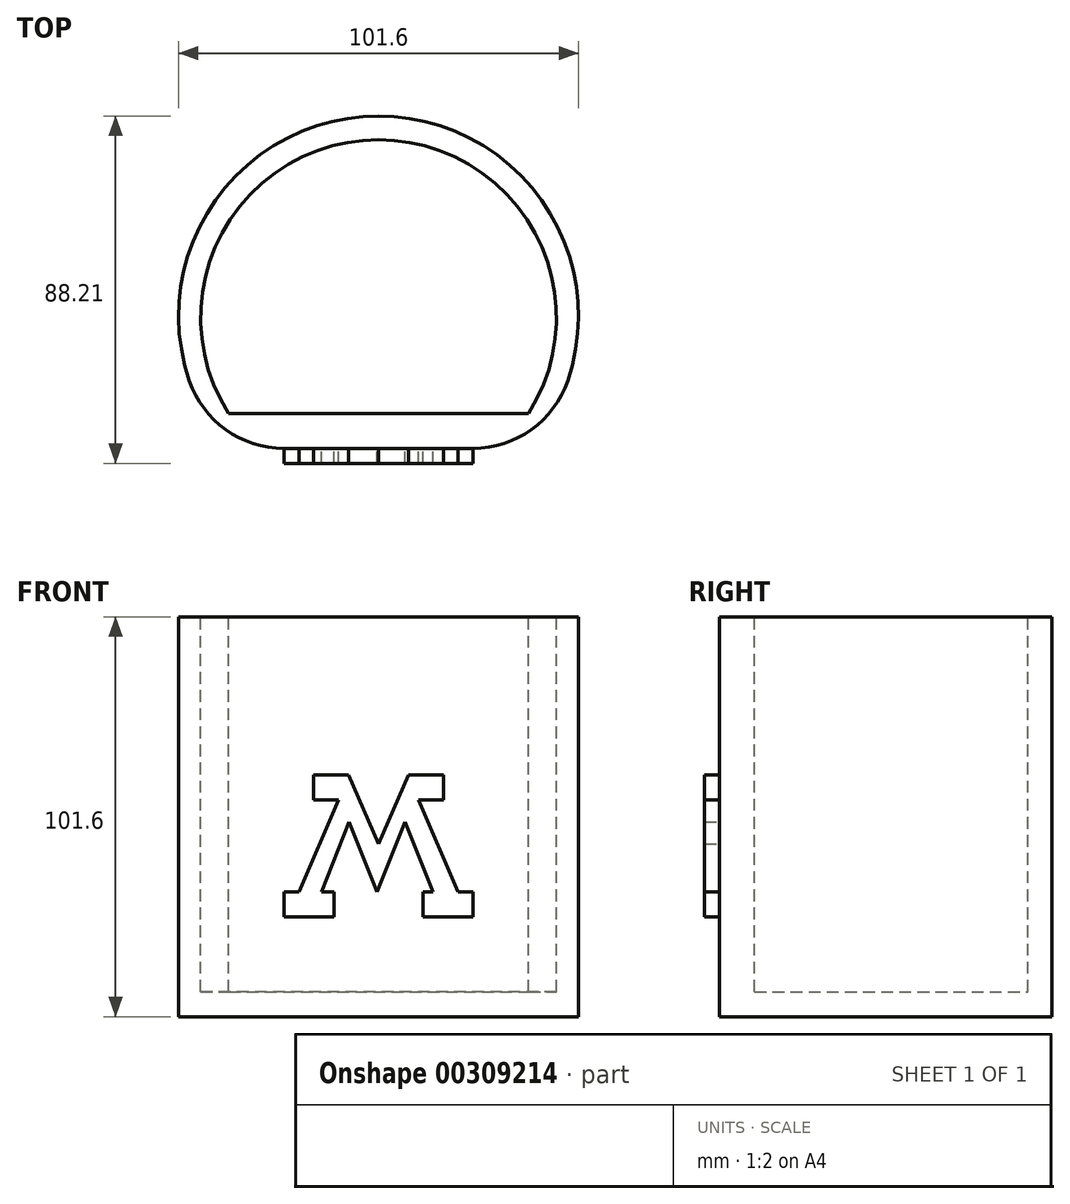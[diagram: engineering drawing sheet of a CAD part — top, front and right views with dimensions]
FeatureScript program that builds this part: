
annotation { "Feature Type Name" : "Feature", "Feature Type Description" : "" }
export const myFeature = defineFeature(function(context is Context, id is Id, definition is map)
    precondition{}
    {
        {
            var Q0;
            Q0=qCreatedBy(makeId("Top.planeOp"),FACE);
            var sketch = newSketch(context, id + "F0", { "sketchPlane" : qUnion([Q0])});
            skLineSegment(sketch, "E0", {"start": v(-42.3, 0) * mm, "end": v(33.9, 0) * mm});
            skArc(sketch, "E1", {"start": v(33.9, 0) * mm, "mid": v(-4.2, 84.4) * mm, "end": v(-42.3, 0) * mm});
            skSolve(sketch);
        }
        {
            var Q0;
            Q0=makeQuery(id+"F0.imprint","IMPRINT",FACE,{"disambiguationData":[TD([[makeQuery(id+"F0.imprint","IMPRINT",EDGE,{"derivedFrom":sQuery(id+"F0.wireOp",EDGE,"E0")}),1.0]])]});
            extrude(context, id + "F1", {"entities" : qUnion([Q0]), "depth" : 101.6 * mm});
        }
        {
            var Q0;
            Q0=makeQuery(id+"F1.opExtrude","CAP_FACE",FACE,{"disambiguationData":[OSD([sQuery(id+"F0.wireOp",EDGE,"E0"),sQuery(id+"F0.wireOp",EDGE,"E1")])],"isStart":false});
            var sketch = newSketch(context, id + "F2", { "sketchPlane" : qUnion([Q0])});
            skLineSegment(sketch, "E2", {"start": v(-42.3, 8.9) * mm, "end": v(33.9, 8.9) * mm});
            skArc(sketch, "E3", {"start": v(33.9, 8.9) * mm, "mid": v(-4.2, 78.39) * mm, "end": v(-42.3, 8.9) * mm});
            skSolve(sketch);
        }
        {
            var Q0;
            Q0=makeQuery(id+"F2.imprint","IMPRINT",FACE,{"disambiguationData":[TD([[makeQuery(id+"F2.imprint","IMPRINT",EDGE,{"derivedFrom":sQuery(id+"F2.wireOp",EDGE,"EuxJ9lTJ-i6S2-fETs-Mgd1-tVgnAVQvERU8")}),1.0]])]});
            var Q1;
            Q1=makeQuery(id+"F2.imprint","IMPRINT",FACE,{"disambiguationData":[TD([[makeQuery(id+"F2.imprint","IMPRINT",EDGE,{"derivedFrom":sQuery(id+"F2.wireOp",EDGE,"E2")}),1.0]])]});
            extrude(context, id + "F3", {"entities" : qUnion([Q0, Q1]), "operationType" : NewBodyOperationType.REMOVE, "oppositeDirection" : true, "depth" : 95.25 * mm});
        }
        {
            var Q0;
            {var subQ0=sQuery(id+"F0.wireOp",EDGE,"E1");var subQ1=sQuery(id+"F0.wireOp",EDGE,"E0");Q0=makeQuery(id+"F1.opExtrude","SWEPT_EDGE",EDGE,{"disambiguationData":[OSD([subQ1,subQ0]),TDD([makeQuery(id+"F0.imprint","INTERSECT",VERTEX,{"disambiguationData":[OD(0.0)],"derivedFrom":[subQ1,subQ0]})])]});}
            var Q1;
            {var subQ0=sQuery(id+"F0.wireOp",EDGE,"E1");var subQ1=sQuery(id+"F0.wireOp",EDGE,"E0");Q1=makeQuery(id+"F1.opExtrude","SWEPT_EDGE",EDGE,{"disambiguationData":[OSD([subQ1,subQ0]),TDD([makeQuery(id+"F0.imprint","INTERSECT",VERTEX,{"disambiguationData":[OD(1.0)],"derivedFrom":[subQ1,subQ0]})])]});}
            fillet(context, id + "F4", {"entities" : qUnion([Q0, Q1]), "radius" : 25.4 * mm, "tangentPropagation" : true, "allowEdgeOverflow" : false});
        }
        {
            var Q0;
            Q0=makeQuery(id+"F1.opExtrude","SWEPT_FACE",FACE,{"disambiguationData":[OSD([sQuery(id+"F0.wireOp",EDGE,"E0")])]});
            var sketch = newSketch(context, id + "F5", { "sketchPlane" : qUnion([Q0])});
            skPoint(sketch, "E4.endSnap0", {"position": v(19.83, 50.8) * mm});
            skLineSegment(sketch, "E5", {"start": v(-28.25, 0) * mm, "end": v(-28.25, 25.4) * mm});
            skLineSegment(sketch, "E6", {"start": v(-28.25, 25.4) * mm, "end": v(-15.55, 25.4) * mm});
            skLineSegment(sketch, "E7", {"start": v(-15.55, 25.4) * mm, "end": v(-15.55, 31.75) * mm});
            skLineSegment(sketch, "E8", {"start": v(-15.55, 31.75) * mm, "end": v(-18.74, 31.75) * mm});
            skLineSegment(sketch, "E9", {"start": v(19.83, 0) * mm, "end": v(19.83, 25.4) * mm});
            skLineSegment(sketch, "E10", {"start": v(19.83, 25.4) * mm, "end": v(7.13, 25.4) * mm});
            skPoint(sketch, "E10.endSnap0", {"position": v(-21.9, 25.4) * mm});
            skLineSegment(sketch, "E11", {"start": v(7.13, 25.4) * mm, "end": v(7.13, 31.75) * mm});
            skLineSegment(sketch, "E12", {"start": v(7.13, 31.75) * mm, "end": v(9.64, 31.75) * mm});
            skLineSegment(sketch, "E13", {"start": v(-18.74, 31.75) * mm, "end": v(-11.64, 49.43) * mm});
            skLineSegment(sketch, "E14", {"start": v(-11.64, 49.43) * mm, "end": v(-4.55, 31.75) * mm});
            skLineSegment(sketch, "E15", {"start": v(-4.55, 31.75) * mm, "end": v(2.55, 49.43) * mm});
            skLineSegment(sketch, "E16", {"start": v(2.55, 49.43) * mm, "end": v(9.64, 31.75) * mm});
            skLineSegment(sketch, "E17", {"start": v(-28.25, 25.4) * mm, "end": v(-28.25, 31.75) * mm});
            skLineSegment(sketch, "E18", {"start": v(-28.25, 31.75) * mm, "end": v(-24.44, 31.75) * mm});
            skLineSegment(sketch, "E19", {"start": v(-24.44, 31.75) * mm, "end": v(-14.33, 55.05) * mm});
            skLineSegment(sketch, "E20", {"start": v(-14.33, 55.05) * mm, "end": v(-20.68, 55.05) * mm});
            skLineSegment(sketch, "E21", {"start": v(-20.68, 55.05) * mm, "end": v(-20.68, 61.4) * mm});
            skLineSegment(sketch, "E22", {"start": v(-20.68, 61.4) * mm, "end": v(-11.79, 61.4) * mm});
            skLineSegment(sketch, "E23", {"start": v(-11.79, 61.4) * mm, "end": v(-4.2, 43.93) * mm});
            skLineSegment(sketch, "E24", {"start": v(-4.2, 43.93) * mm, "end": v(3.37, 61.4) * mm});
            skLineSegment(sketch, "E25", {"start": v(3.37, 61.4) * mm, "end": v(12.26, 61.4) * mm});
            skLineSegment(sketch, "E26", {"start": v(12.26, 61.4) * mm, "end": v(12.26, 55.05) * mm});
            skLineSegment(sketch, "E27", {"start": v(12.26, 55.05) * mm, "end": v(5.91, 55.05) * mm});
            skLineSegment(sketch, "E28", {"start": v(5.91, 55.05) * mm, "end": v(16.02, 31.75) * mm});
            skLineSegment(sketch, "E29", {"start": v(16.02, 31.75) * mm, "end": v(19.83, 31.75) * mm});
            skSolve(sketch);
        }
        {
            var Q0;
            Q0=makeQuery(id+"F5.imprint","IMPRINT",FACE,{"disambiguationData":[TD([[makeQuery(id+"F5.imprint","IMPRINT",EDGE,{"derivedFrom":sQuery(id+"F5.wireOp",EDGE,"E6")}),1.0]])]});
            extrude(context, id + "F6", {"entities" : qUnion([Q0]), "operationType" : NewBodyOperationType.ADD, "depth" : 3.8 * mm});
        }
    });
